# Revit family: Haworth_HC1Pedestal_7HE_EU_PRELIMINARY
name_source: partatom
category: Furniture Systems
units: mm (PartAtom-declared; Revit-internal decimal feet)

## family parameters
Always vertical = Yes
Cut with Voids When Loaded = No
OmniClass Number = 23.40.70.14.64.21
OmniClass Title = Systems Furniture
Part Type = Normal
Room Calculation Point = No
Round Connector Dimension = Use Diameter
Shared = No
Work Plane-Based = No

## types (1)
- 1/3/3 43.3 x 60 x 41.6
    60D Top = Yes
    70D Top = No
    Actual Depth = 60 cm
    Actual Height = 42 cm
    Actual Width = 43 cm
    Assembly Code = E2020200
    Casters = No
    Description = Haworth - HC1 Pedestal - 7HE Pedestal
    Glide Finish = Haworth _ Polymer _ Black
    Glides = Yes
    Handle 1 = No
    Handle 128 128 = Yes
    Handle 2 = No
    Handle Metal = No
    High = Yes
    Low = No
    Manufacturer = Haworth
    Model = MS706133
    Pull Finish = Haworth _ Paint _ Smooth Plaster
    Recessed Handle 128 = No
    Revision Number = 1
    Size = Verify Final Dim. w/ Haworth
    Standard Handle 1 = No
    Standard Handle 2 = No
    Thickness = 3 cm
    Top Depth = 60 cm
    URL = https://www.haworth.com
    URL - Product = https://www.haworth.com
    Warranty = http://www.haworth.com
    Without Pull = No

## geometry (parser evidence)
native form markers: Sweep x24
no freeform markers — native parametric forms only
